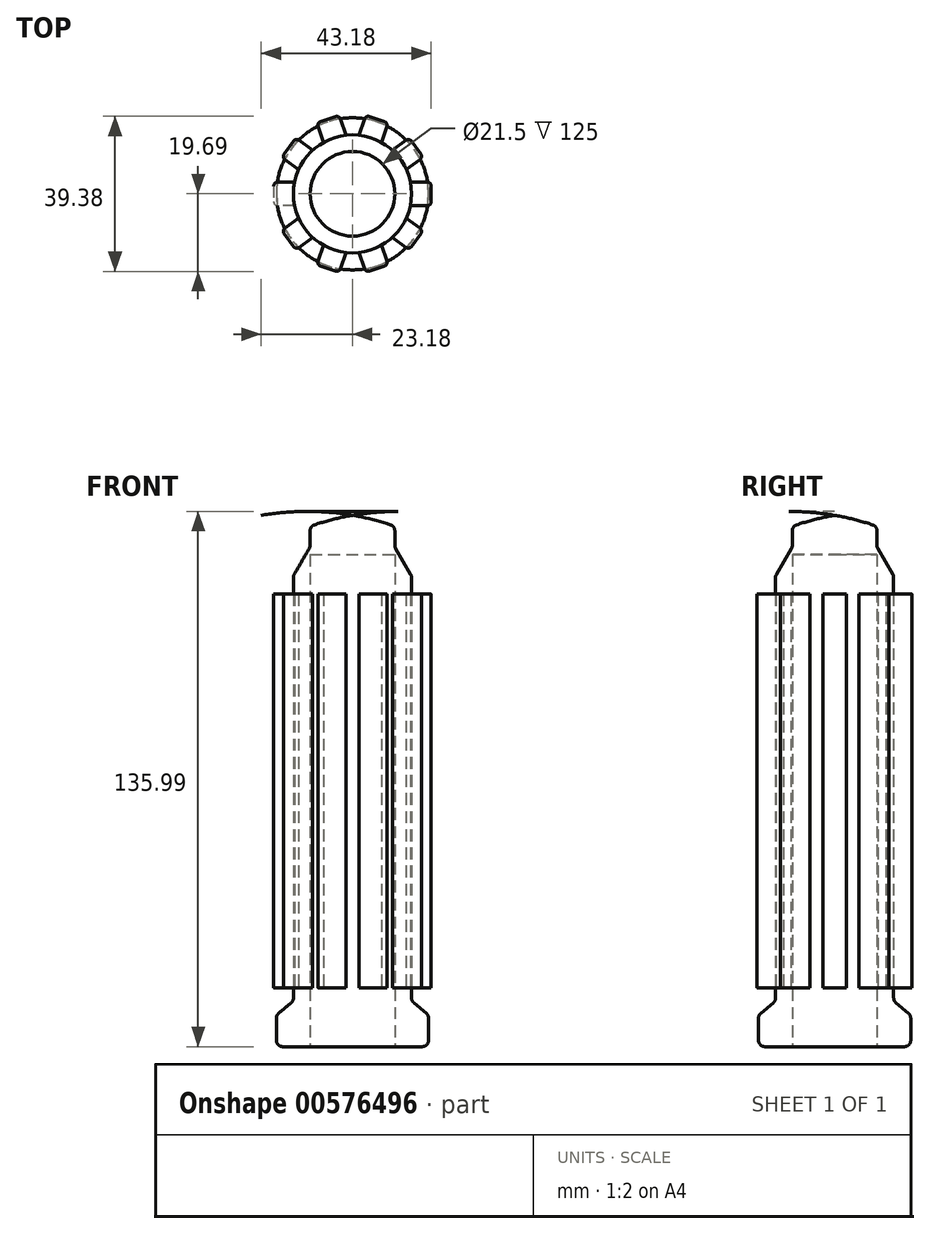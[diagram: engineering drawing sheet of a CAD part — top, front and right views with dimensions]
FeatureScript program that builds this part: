
annotation { "Feature Type Name" : "Feature", "Feature Type Description" : "" }
export const myFeature = defineFeature(function(context is Context, id is Id, definition is map)
    precondition{}
    {
        {
            var Q0;
            Q0=qCreatedBy(makeId("Front.planeOp"),FACE);
            var sketch = newSketch(context, id + "F0", { "sketchPlane" : qUnion([Q0])});
            skLineSegment(sketch, "E0", {"start": v(10.75, 0) * mm, "end": v(19.32, 0) * mm});
            skLineSegment(sketch, "E1", {"start": v(19.32, 0) * mm, "end": v(19.32, 8) * mm});
            skLineSegment(sketch, "E2", {"start": v(19.32, 8) * mm, "end": v(15, 11.63) * mm});
            skLineSegment(sketch, "E3", {"start": v(15, 11.63) * mm, "end": v(15, 119.64) * mm});
            skLineSegment(sketch, "E4", {"start": v(15, 119.64) * mm, "end": v(10.75, 127) * mm});
            skLineSegment(sketch, "E5", {"start": v(10.75, 127) * mm, "end": v(10.75, 132.22) * mm});
            skLineSegment(sketch, "E6", {"start": v(10.75, 0) * mm, "end": v(10.75, 125) * mm});
            skLineSegment(sketch, "E7", {"start": v(10.75, 125) * mm, "end": v(0, 125) * mm});
            skLineSegment(sketch, "E8", {"start": v(0, 125) * mm, "end": v(0, 135) * mm});
            skArc(sketch, "E9", {"start": v(10.75, 132.22) * mm, "mid": v(5.43, 133.83) * mm, "end": v(0, 135) * mm});
            skSolve(sketch);
        }
        {
            var Q0;
            Q0=makeQuery(id+"F0.imprint","IMPRINT",FACE,{"disambiguationData":[TD([[makeQuery(id+"F0.imprint","IMPRINT",EDGE,{"derivedFrom":sQuery(id+"F0.wireOp",EDGE,"E0")}),1.0]])]});
            var Q1;
            Q1=sQuery(id+"F0.wireOp",EDGE,"E8");
            revolve(context, id + "F1", {"surfaceOperationType" : NewSurfaceOperationType.NEW, "entities" : qUnion([Q0]), "axis" : qUnion([Q1]), "revolveType" : RevolveType.FULL});
        }
        {
            var Q0;
            Q0=makeQuery(id+"F1.opRevolve","SWEPT_EDGE",EDGE,{"disambiguationData":[OSD([sQuery(id+"F0.wireOp",EDGE,"E3"),sQuery(id+"F0.wireOp",EDGE,"E4")])]});
            var Q1;
            Q1=makeQuery(id+"F1.opRevolve","SWEPT_EDGE",EDGE,{"disambiguationData":[OSD([sQuery(id+"F0.wireOp",EDGE,"E4"),sQuery(id+"F0.wireOp",EDGE,"E5")])]});
            var Q2;
            Q2=makeQuery(id+"F1.opRevolve","SWEPT_EDGE",EDGE,{"disambiguationData":[OSD([sQuery(id+"F0.wireOp",EDGE,"E5"),sQuery(id+"F0.wireOp",EDGE,"E9")])]});
            var Q3;
            Q3=makeQuery(id+"F1.opRevolve","SWEPT_EDGE",EDGE,{"disambiguationData":[OSD([sQuery(id+"F0.wireOp",EDGE,"E1"),sQuery(id+"F0.wireOp",EDGE,"E2")])]});
            var Q4;
            Q4=makeQuery(id+"F1.opRevolve","SWEPT_EDGE",EDGE,{"disambiguationData":[OSD([sQuery(id+"F0.wireOp",EDGE,"E0"),sQuery(id+"F0.wireOp",EDGE,"E1")])]});
            var Q5;
            Q5=makeQuery(id+"F1.opRevolve","SWEPT_EDGE",EDGE,{"disambiguationData":[OSD([sQuery(id+"F0.wireOp",EDGE,"E2"),sQuery(id+"F0.wireOp",EDGE,"E3")])]});
            fillet(context, id + "F2", {"entities" : qUnion([Q0, Q1, Q2, Q3, Q4, Q5]), "radius" : 1.6 * mm, "tangentPropagation" : true, "allowEdgeOverflow" : false});
        }
        {
            var Q0;
            Q0=qCreatedBy(makeId("Right.planeOp"),FACE);
            cPlane(context, id + "F3", {"entities" : qUnion([Q0]), "cplaneType" : CPlaneType.OFFSET, "offset" : 20 * mm, "width" : 150 * mm, "height" : 150 * mm});
        }
        {
            var Q0;
            Q0=qCreatedBy(id+"F3.planeOp",FACE);
            var sketch = newSketch(context, id + "F4", { "sketchPlane" : qUnion([Q0])});
            skLineSegment(sketch, "E10.bottom", {"start": v(-3, 15) * mm, "end": v(3, 15) * mm});
            skLineSegment(sketch, "E10.top", {"start": v(-3, 115) * mm, "end": v(3, 115) * mm});
            skLineSegment(sketch, "E10.left", {"start": v(-3, 15) * mm, "end": v(-3, 115) * mm});
            skLineSegment(sketch, "E10.right", {"start": v(3, 15) * mm, "end": v(3, 115) * mm});
            skSolve(sketch);
        }
        {
            var Q0;
            Q0 = qSketchRegion(id + "F4", true);
            var Q1;
            Q1=makeQuery(id+"F1.opRevolve","SWEPT_FACE",FACE,{"disambiguationData":[OSD([sQuery(id+"F0.wireOp",EDGE,"E3")])]});
            extrude(context, id + "F5", {"entities" : qUnion([Q0]), "endBound" : BoundingType.UP_TO_SURFACE, "oppositeDirection" : true, "depth" : 25 * mm, "endBoundEntityFace" : qUnion([Q1]), "offsetDistance" : 25 * mm});
        }
        {
            var Q0;
            Q0=makeQuery(id+"F5.opExtrude","CAP_EDGE",EDGE,{"disambiguationData":[OSD([sQuery(id+"F4.wireOp",EDGE,"E10.left")])],"isStart":true});
            var Q1;
            Q1=makeQuery(id+"F5.opExtrude","CAP_EDGE",EDGE,{"disambiguationData":[OSD([sQuery(id+"F4.wireOp",EDGE,"E10.right")])],"isStart":true});
            fillet(context, id + "F6", {"entities" : qUnion([Q0, Q1]), "radius" : 1 * mm, "tangentPropagation" : true, "allowEdgeOverflow" : false});
        }
        {
            var Q0;
            Q0=makeQuery(id+"F5.opExtrude","SWEPT_BODY",BODY,{"disambiguationData":[OSD([sQuery(id+"F4.wireOp",EDGE,"E10.bottom"),sQuery(id+"F4.wireOp",EDGE,"E10.top"),sQuery(id+"F4.wireOp",EDGE,"E10.left"),sQuery(id+"F4.wireOp",EDGE,"E10.right")])]});
            var Q1;
            Q1=makeQuery(id+"F1.opRevolve","SWEPT_FACE",FACE,{"disambiguationData":[OSD([sQuery(id+"F0.wireOp",EDGE,"E3")])]});
            circularPattern(context, id + "F7", {"entities" : qUnion([Q0]), "axis" : qUnion([Q1]), "angle" : 360 * degree, "instanceCount" : 10, "equalSpace" : true});
        }
    });
